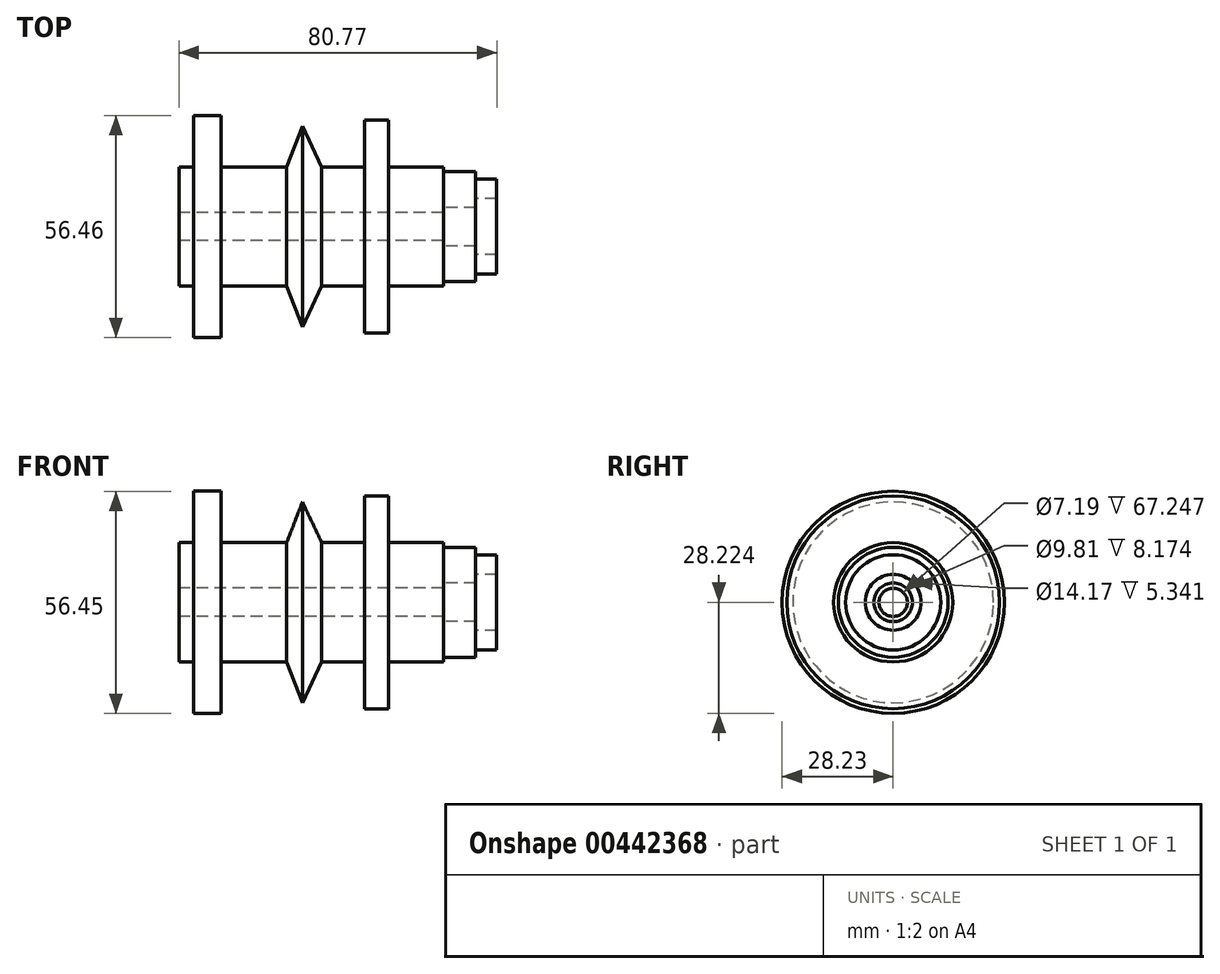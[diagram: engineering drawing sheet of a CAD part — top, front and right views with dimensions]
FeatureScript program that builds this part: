
annotation { "Feature Type Name" : "Feature", "Feature Type Description" : "" }
export const myFeature = defineFeature(function(context is Context, id is Id, definition is map)
    precondition{}
    {
        {
            var Q0;
            Q0=qCreatedBy(makeId("Front.planeOp"),FACE);
            var sketch = newSketch(context, id + "F0", { "sketchPlane" : qUnion([Q0])});
            skLineSegment(sketch, "E0.bottom", {"start": v(-33.79, 16.94) * mm, "end": v(-30.08, 16.94) * mm});
            skLineSegment(sketch, "E0.top", {"start": v(-33.79, 5.4) * mm, "end": v(33.46, 5.4) * mm});
            skLineSegment(sketch, "E0.left", {"start": v(-33.79, 16.94) * mm, "end": v(-33.79, 5.4) * mm});
            skLineSegment(sketch, "E0.right", {"start": v(33.46, 16.94) * mm, "end": v(33.46, 15.74) * mm});
            skLineSegment(sketch, "E1.bottom", {"start": v(-30.08, 30.02) * mm, "end": v(-23.1, 30.02) * mm});
            skLineSegment(sketch, "E1.left", {"start": v(-30.08, 30.02) * mm, "end": v(-30.08, 16.94) * mm});
            skLineSegment(sketch, "E1.right", {"start": v(-23.1, 30.02) * mm, "end": v(-23.1, 16.94) * mm});
            skLineSegment(sketch, "E2", {"start": v(-6.43, 16.83) * mm, "end": v(-2.4, 27.3) * mm});
            skLineSegment(sketch, "E3", {"start": v(-2.4, 27.3) * mm, "end": v(2.5, 16.94) * mm});
            skLineSegment(sketch, "E4.bottom", {"start": v(13.4, 28.82) * mm, "end": v(19.5, 28.82) * mm});
            skLineSegment(sketch, "E4.top", {"start": v(13.4, 16.94) * mm, "end": v(19.5, 16.94) * mm});
            skLineSegment(sketch, "E4.left", {"start": v(13.4, 28.82) * mm, "end": v(13.4, 16.94) * mm});
            skLineSegment(sketch, "E4.right", {"start": v(19.5, 28.82) * mm, "end": v(19.5, 16.94) * mm});
            skLineSegment(sketch, "E5.bottom", {"start": v(33.46, 15.74) * mm, "end": v(41.63, 15.74) * mm});
            skLineSegment(sketch, "E5.top", {"start": v(33.46, 6.7) * mm, "end": v(41.63, 6.7) * mm});
            skLineSegment(sketch, "E5.right", {"start": v(41.63, 15.74) * mm, "end": v(41.63, 13.9) * mm});
            skLineSegment(sketch, "E6.bottom", {"start": v(41.63, 13.9) * mm, "end": v(46.98, 13.9) * mm});
            skLineSegment(sketch, "E6.top", {"start": v(41.63, 8.88) * mm, "end": v(46.98, 8.88) * mm});
            skLineSegment(sketch, "E6.right", {"start": v(46.98, 13.9) * mm, "end": v(46.98, 8.88) * mm});
            skLineSegment(sketch, "E7", {"start": v(-36.73, 1.8) * mm, "end": v(48.28, 1.8) * mm});
            skLineSegment(sketch, "E8.trimOffspring", {"start": v(-23.1, 16.94) * mm, "end": v(-6.39, 16.94) * mm});
            skLineSegment(sketch, "E9.trimOffspring", {"start": v(2.5, 16.94) * mm, "end": v(13.4, 16.94) * mm});
            skLineSegment(sketch, "E10.trimOffspring", {"start": v(19.5, 16.94) * mm, "end": v(33.46, 16.94) * mm});
            skLineSegment(sketch, "E11.trimOffspring", {"start": v(33.46, 6.7) * mm, "end": v(33.46, 5.4) * mm});
            skLineSegment(sketch, "E12.trimOffspring", {"start": v(41.63, 8.88) * mm, "end": v(41.63, 6.7) * mm});
            skSolve(sketch);
        }
        {
            var Q0;
            Q0 = qSketchRegion(id + "F0", true);
            var Q1;
            Q1=sQuery(id+"F0.wireOp",EDGE,"E7");
            revolve(context, id + "F1", {"entities" : qUnion([Q0]), "axis" : qUnion([Q1]), "revolveType" : RevolveType.FULL});
        }
    });
